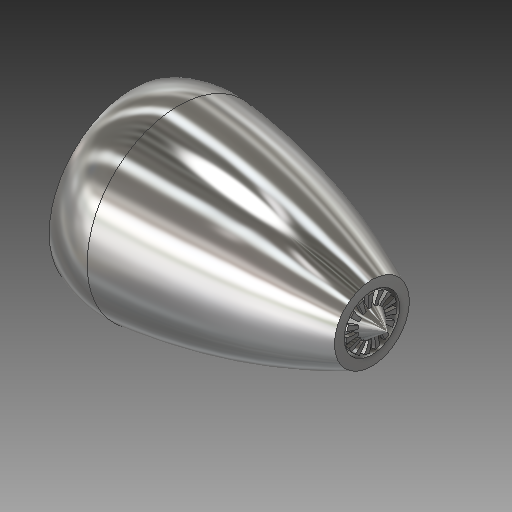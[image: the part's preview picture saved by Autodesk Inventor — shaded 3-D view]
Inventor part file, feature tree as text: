
AUTODESK INVENTOR PART (.ipt)
format: ipt  version: 2018 (Build 220112000, 112)  size: 564,736 bytes
history: native  units: in
note: dims shown in document units (in); Inventor stores cm internally (conversion verified against a paired STEP export)
features: sketch x18, extrude x6, plane x5, revolve x4, pattern_circular x2
ambient origin geometry x8: Origin, YZ Plane, XZ Plane, XY Plane, X Axis, Y Axis, Z Axis, Center Point
bodies: Solid1 (feature_tree)
feature tree (35):
  revolve  "Revolution1"  Angle=90.0deg
  sketch  "Sketch2"  dims[d2=180.0deg d3=1.1811in]
  sketch  "Sketch3"  dims[d4=1.063in d5=1.378in]
  sketch  "Sketch4"  dims[d6=1.5748in d7=0.4331in d8=0.0in d9=0.0in d10=2.9528in]
  revolve  "Revolution2"  [1 undecoded]
  plane  "Work Plane1"
  sketch  "Sketch5"  dims[d11=3.1496in d12=0.0in d13=1.378in]
  plane  "Work Plane2"
  extrude  "Extrusion1"  Depth=1.378in
  sketch  "Sketch7"  dims[d17=1.5748in d18=0.0in d19=180.0deg]
  extrude  "Extrusion2"  Depth=2.9528in
  extrude  "Extrusion3"  Depth=1.378in
  extrude  "Extrusion4"  Depth=2.3622in
  sketch  "Sketch11"  dims[d39=180.0deg]
  revolve  "Revolution3"  Angle=180.0deg
  plane  "Work Plane3"
  extrude  "Extrusion5"  Depth=0.1969in TaperAngle=0.0deg
  sketch  "Sketch14"
  pattern_circular  "Circular Pattern1"  Count=15 Angle=360.0deg
  plane  "Work Plane4"
  sketch  "Sketch15"
  plane  "Work Plane5"
  extrude  "Extrusion6"  TaperAngle=0.0deg  [1 undecoded]
  pattern_circular  "Circular Pattern2"  Count=15 Angle=360.0deg
  revolve  "Revolution4"  [1 undecoded]
  sketch  "Sketch18"
  sketch  "Sketch1"  dims[d0=2.9528in d1=90.0deg]
  sketch  "Sketch6"  dims[d14=1.9685in d15=0.0in d16=2.3622in]
  sketch  "Sketch8"  dims[d20=-2.1654in d23=0.1969in d24=0.0in d25=5.9055in d26=360.0deg]
  sketch  "Sketch9"  dims[d28=0.5906in d29=0.0in]
  sketch  "Sketch10"  dims[d32=0.3937in d33=0.0in d34=5.9055in d35=360.0deg]
  sketch  "Sketch12"
  sketch  "Sketch13"
  sketch  "Sketch16"
  sketch  "Sketch17"
note: 3 required parameter values undecoded (feature->parameter linkage not recoverable at this tier; creation-order binding heuristic only, values carry confidence <= 0.55)